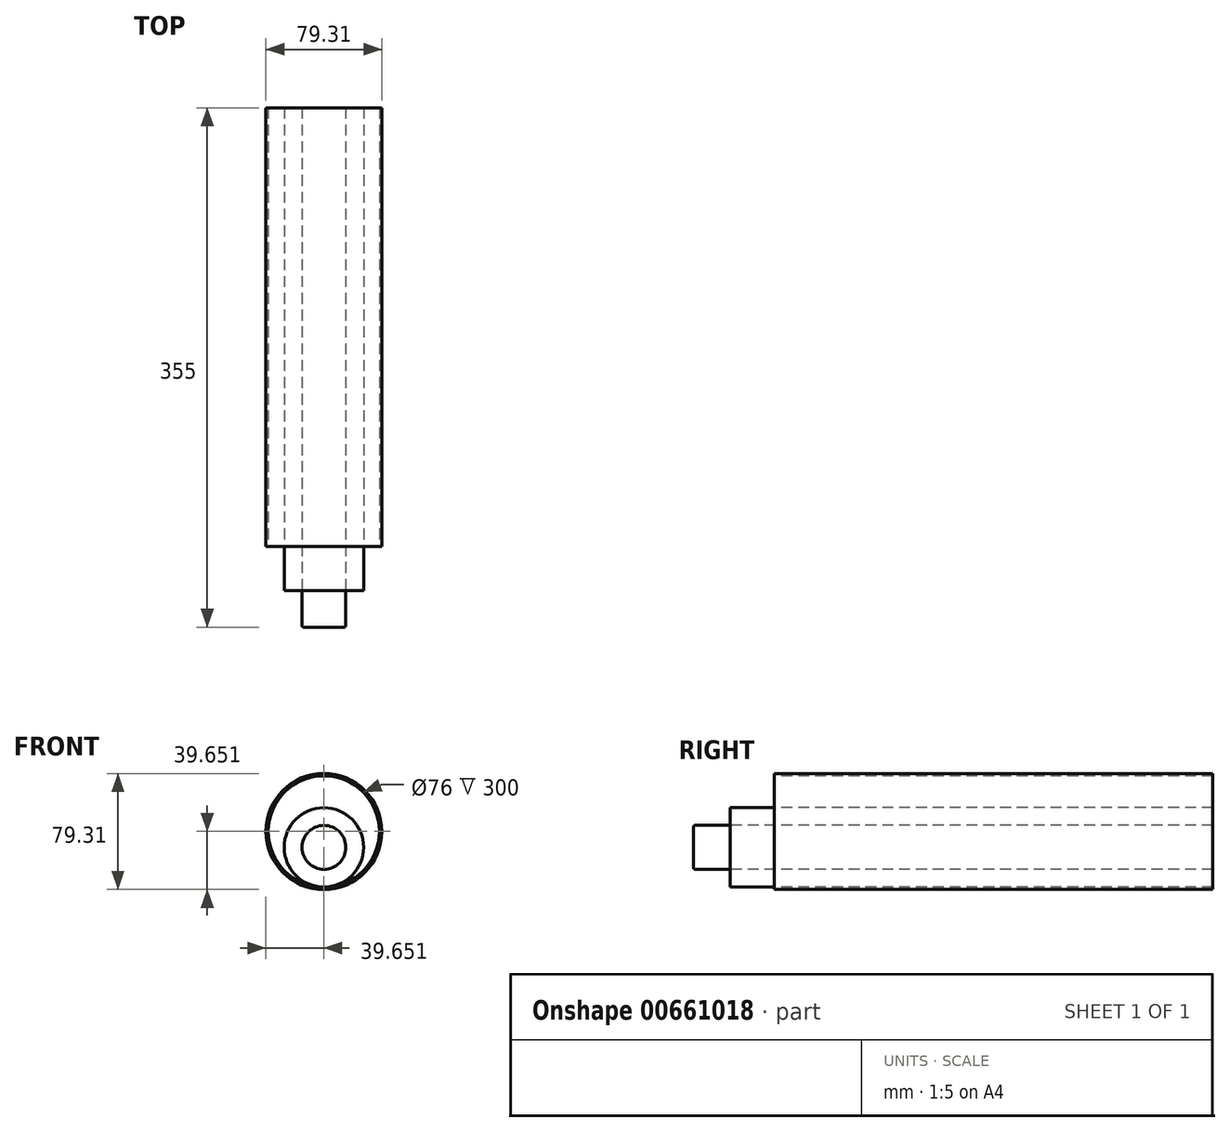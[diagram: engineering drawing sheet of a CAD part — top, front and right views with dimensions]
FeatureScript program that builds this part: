
annotation { "Feature Type Name" : "Feature", "Feature Type Description" : "" }
export const myFeature = defineFeature(function(context is Context, id is Id, definition is map)
    precondition{}
    {
        {
            var Q0;
            Q0=qCreatedBy(makeId("Front.planeOp"),FACE);
            var sketch = newSketch(context, id + "F0", { "sketchPlane" : qUnion([Q0])});
            skCircle(sketch, "E0", {"center": v(-58.59, 37.11) * mm, "radius": 38 * mm});
            skCircle(sketch, "E1", {"center": v(-58.59, 26.25) * mm, "radius": 27.14 * mm});
            skCircle(sketch, "E2", {"center": v(-58.59, 26.25) * mm, "radius": 15 * mm});
            skCircle(sketch, "E3", {"center": v(-58.59, 37.11) * mm, "radius": 39.66 * mm});
            skSolve(sketch);
        }
        {
            var Q0;
            Q0=makeQuery(id+"F0.imprint","IMPRINT",FACE,{"disambiguationData":[TD([[makeQuery(id+"F0.imprint","IMPRINT",EDGE,{"derivedFrom":sQuery(id+"F0.wireOp",EDGE,"E3")}),1.0]])]});
            extrude(context, id + "F1", {"entities" : qUnion([Q0]), "oppositeDirection" : true, "depth" : 300 * mm, "offsetDistance" : 25 * mm});
        }
        {
            var Q0;
            Q0=makeQuery(id+"F0.imprint","IMPRINT",FACE,{"disambiguationData":[TD([[makeQuery(id+"F0.imprint","IMPRINT",EDGE,{"derivedFrom":sQuery(id+"F0.wireOp",EDGE,"E2")}),-1.0]])]});
            var Q1;
            Q1=makeQuery(id+"F0.imprint","IMPRINT",FACE,{"disambiguationData":[TD([[makeQuery(id+"F0.imprint","IMPRINT",EDGE,{"derivedFrom":sQuery(id+"F0.wireOp",EDGE,"qjIUl3Bz-GJGD-Cghm-fR1f-TL6YvNrD2wQO")}),-1.0]])]});
            var Q2;
            Q2=makeQuery(id+"F0.imprint","IMPRINT",FACE,{"disambiguationData":[TD([[makeQuery(id+"F0.imprint","IMPRINT",EDGE,{"derivedFrom":sQuery(id+"F0.wireOp",EDGE,"rnlIIN14-UW7n-WpoC-Pdel-Fr4G14prvleX")}),-1.0]])]});
            extrude(context, id + "F2", {"entities" : qUnion([Q0, Q1, Q2]), "operationType" : NewBodyOperationType.ADD, "oppositeDirection" : true, "depth" : 300 * mm, "offsetDistance" : 25 * mm, "hasSecondDirection" : true, "secondDirectionOppositeDirection" : false, "secondDirectionDepth" : 30 * mm});
        }
        {
            var Q0;
            Q0=makeQuery(id+"F0.imprint","IMPRINT",FACE,{"disambiguationData":[TD([[makeQuery(id+"F0.imprint","IMPRINT",EDGE,{"derivedFrom":sQuery(id+"F0.wireOp",EDGE,"E2")}),1.0]])]});
            var Q1;
            Q1=makeQuery(id+"F0.imprint","IMPRINT",FACE,{"disambiguationData":[TD([[makeQuery(id+"F0.imprint","IMPRINT",EDGE,{"derivedFrom":sQuery(id+"F0.wireOp",EDGE,"qjIUl3Bz-GJGD-Cghm-fR1f-TL6YvNrD2wQO")}),1.0]])]});
            var Q2;
            Q2=makeQuery(id+"F0.imprint","IMPRINT",FACE,{"disambiguationData":[TD([[makeQuery(id+"F0.imprint","IMPRINT",EDGE,{"derivedFrom":sQuery(id+"F0.wireOp",EDGE,"rnlIIN14-UW7n-WpoC-Pdel-Fr4G14prvleX")}),1.0]])]});
            extrude(context, id + "F3", {"entities" : qUnion([Q0, Q1, Q2]), "oppositeDirection" : true, "depth" : 300 * mm, "offsetDistance" : 25 * mm, "hasSecondDirection" : true, "secondDirectionOppositeDirection" : false, "secondDirectionDepth" : 55 * mm});
        }
        {
            var Q0;
            Q0=makeQuery(id+"F3.opExtrude","CAP_EDGE",EDGE,{"disambiguationData":[OSD([sQuery(id+"F0.wireOp",EDGE,"E2")])],"isStart":true});
            var Q1;
            Q1=makeQuery(id+"F3.opExtrude","CAP_EDGE",EDGE,{"disambiguationData":[OSD([sQuery(id+"F0.wireOp",EDGE,"qjIUl3Bz-GJGD-Cghm-fR1f-TL6YvNrD2wQO")])],"isStart":true});
            var Q2;
            Q2=makeQuery(id+"F3.opExtrude","CAP_EDGE",EDGE,{"disambiguationData":[OSD([sQuery(id+"F0.wireOp",EDGE,"rnlIIN14-UW7n-WpoC-Pdel-Fr4G14prvleX")])],"isStart":true});
            fillet(context, id + "F4", {"entities" : qUnion([Q0, Q1, Q2]), "radius" : 1 * mm, "tangentPropagation" : true, "allowEdgeOverflow" : false});
        }
    });
